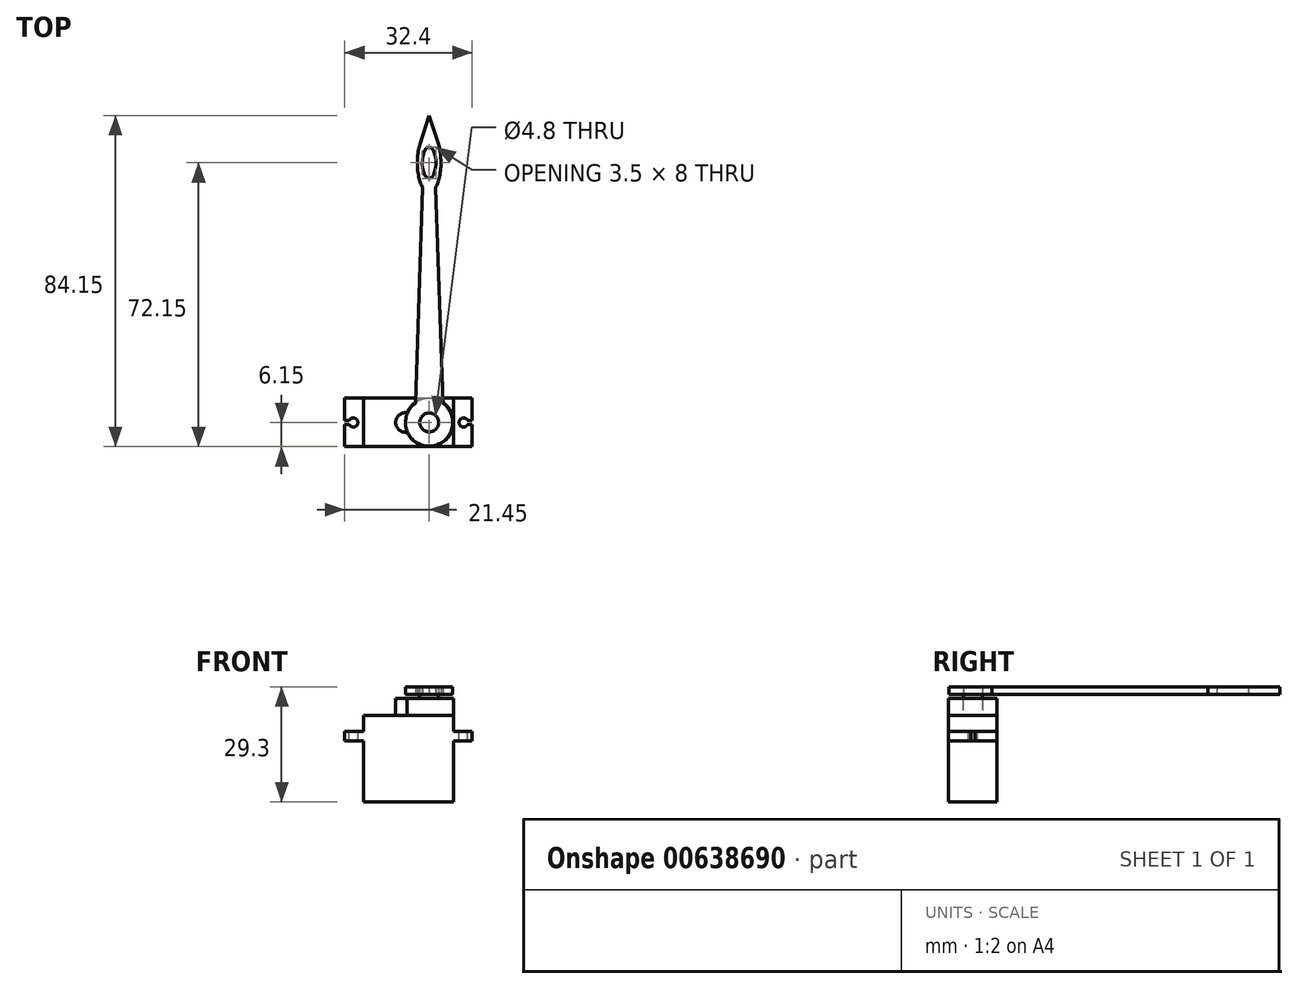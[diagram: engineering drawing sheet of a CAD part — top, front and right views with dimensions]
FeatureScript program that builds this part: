
annotation { "Feature Type Name" : "Feature", "Feature Type Description" : "" }
export const myFeature = defineFeature(function(context is Context, id is Id, definition is map)
    precondition{}
    {
        {
            var Q0;
            Q0=qCreatedBy(makeId("Top.planeOp"),FACE);
            var sketch = newSketch(context, id + "F0", { "sketchPlane" : qUnion([Q0])});
            skLineSegment(sketch, "E0.bottom", {"start": v(0, 0) * mm, "end": v(22.8, 0) * mm});
            skLineSegment(sketch, "E0.top", {"start": v(0, 12.3) * mm, "end": v(22.8, 12.3) * mm});
            skLineSegment(sketch, "E0.left", {"start": v(0, 0) * mm, "end": v(0, 12.3) * mm});
            skLineSegment(sketch, "E0.right", {"start": v(22.8, 0) * mm, "end": v(22.8, 12.3) * mm});
            skSolve(sketch);
        }
        {
            var Q0;
            Q0 = qSketchRegion(id + "F0", true);
            extrude(context, id + "F1", {"entities" : qUnion([Q0]), "depth" : 18 * mm, "offsetDistance" : 25 * mm});
        }
        {
            var Q0;
            Q0=makeQuery(id+"F1.opExtrude","CAP_FACE",FACE,{"disambiguationData":[OSD([sQuery(id+"F0.wireOp",EDGE,"E0.bottom"),sQuery(id+"F0.wireOp",EDGE,"E0.top"),sQuery(id+"F0.wireOp",EDGE,"E0.left"),sQuery(id+"F0.wireOp",EDGE,"E0.right")])],"isStart":false});
            var sketch = newSketch(context, id + "F2", { "sketchPlane" : qUnion([Q0])});
            skLineSegment(sketch, "E1.0", {"start": v(0, 12.3) * mm, "end": v(22.8, 12.3) * mm});
            skLineSegment(sketch, "E2.0", {"start": v(0, 0) * mm, "end": v(22.8, 0) * mm});
            skLineSegment(sketch, "E3", {"start": v(0, 12.3) * mm, "end": v(-4.8, 12.3) * mm});
            skLineSegment(sketch, "E4", {"start": v(-4.8, 12.3) * mm, "end": v(-4.8, 6.65) * mm});
            skLineSegment(sketch, "E5", {"start": v(-4.8, 0) * mm, "end": v(0, 0) * mm});
            skLineSegment(sketch, "E6", {"start": v(22.8, 0) * mm, "end": v(27.6, 0) * mm});
            skLineSegment(sketch, "E7", {"start": v(27.6, 0) * mm, "end": v(27.6, 5.65) * mm});
            skLineSegment(sketch, "E8", {"start": v(27.6, 12.3) * mm, "end": v(22.8, 12.3) * mm});
            skArc(sketch, "E9", {"start": v(-3.64, 5.65) * mm, "mid": v(-1.45, 6.15) * mm, "end": v(-3.64, 6.65) * mm});
            skArc(sketch, "E10", {"start": v(26.44, 6.65) * mm, "mid": v(24.25, 6.15) * mm, "end": v(26.44, 5.65) * mm});
            skPoint(sketch, "E10.centerSnap0", {"position": v(22.8, 6.15) * mm});
            skLineSegment(sketch, "E11", {"start": v(-2.6, 6.15) * mm, "end": v(25.4, 6.15) * mm, "construction": true});
            skLineSegment(sketch, "E12", {"start": v(11.4, 6.15) * mm, "end": v(11.4, 12.3) * mm, "construction": true});
            skLineSegment(sketch, "E13", {"start": v(-4.8, 6.65) * mm, "end": v(-3.64, 6.65) * mm});
            skLineSegment(sketch, "E14", {"start": v(-4.8, 5.65) * mm, "end": v(-3.64, 5.65) * mm});
            skLineSegment(sketch, "E15", {"start": v(26.44, 6.65) * mm, "end": v(27.6, 6.65) * mm});
            skLineSegment(sketch, "E16", {"start": v(26.44, 5.65) * mm, "end": v(27.6, 5.65) * mm});
            skLineSegment(sketch, "E17.trimOffspring", {"start": v(-4.8, 5.65) * mm, "end": v(-4.8, 0) * mm});
            skLineSegment(sketch, "E18.trimOffspring", {"start": v(27.6, 6.65) * mm, "end": v(27.6, 12.3) * mm});
            skSolve(sketch);
        }
        {
            var Q0;
            Q0 = qSketchRegion(id + "F2", true);
            extrude(context, id + "F3", {"entities" : qUnion([Q0]), "operationType" : NewBodyOperationType.ADD, "oppositeDirection" : true, "depth" : 2.5 * mm, "offsetDistance" : 25 * mm});
        }
        {
            var Q0;
            Q0=makeQuery(id+"F3.boolean.opBoolean","MERGE",FACE,{"derivedFrom":[makeQuery(id+"F1.opExtrude","CAP_FACE",FACE,{"disambiguationData":[OSD([sQuery(id+"F0.wireOp",EDGE,"E0.bottom"),sQuery(id+"F0.wireOp",EDGE,"E0.top"),sQuery(id+"F0.wireOp",EDGE,"E0.left"),sQuery(id+"F0.wireOp",EDGE,"E0.right")])],"isStart":false}),makeQuery(id+"F3.opExtrude","CAP_FACE",FACE,{"disambiguationData":[OSD([sQuery(id+"F2.wireOp",EDGE,"E1.0"),sQuery(id+"F2.wireOp",EDGE,"E2.0"),sQuery(id+"F2.wireOp",EDGE,"E3"),sQuery(id+"F2.wireOp",EDGE,"E4"),sQuery(id+"F2.wireOp",EDGE,"E5"),sQuery(id+"F2.wireOp",EDGE,"E6"),sQuery(id+"F2.wireOp",EDGE,"E7"),sQuery(id+"F2.wireOp",EDGE,"E8"),sQuery(id+"F2.wireOp",EDGE,"E9"),sQuery(id+"F2.wireOp",EDGE,"E10")])],"isStart":true})]});
            var sketch = newSketch(context, id + "F4", { "sketchPlane" : qUnion([Q0])});
            skLineSegment(sketch, "E19.0", {"start": v(22.8, 0) * mm, "end": v(22.8, 12.3) * mm});
            skLineSegment(sketch, "E20.0", {"start": v(0, 0) * mm, "end": v(0, 12.3) * mm});
            skSolve(sketch);
        }
        {
            var Q0;
            {var subQ0=sQuery(id+"F4.wireOp",EDGE,"E19.0");Q0=makeQuery(id+"F4.imprint","IMPRINT",FACE,{"disambiguationData":[TD([[makeQuery(id+"F4.imprint","IMPRINT",EDGE,{"derivedFrom":subQ0}),1.0]])]});}
            extrude(context, id + "F5", {"entities" : qUnion([Q0]), "operationType" : NewBodyOperationType.ADD, "depth" : 4 * mm, "offsetDistance" : 25 * mm});
        }
        {
            var Q0;
            Q0=makeQuery(id+"F5.opExtrude","CAP_FACE",FACE,{"disambiguationData":[OSD([sQuery(id+"F0.wireOp",EDGE,"E0.bottom"),sQuery(id+"F0.wireOp",EDGE,"E0.top"),sQuery(id+"F2.wireOp",EDGE,"E1.0"),sQuery(id+"F2.wireOp",EDGE,"E2.0"),sQuery(id+"F2.wireOp",EDGE,"E3"),sQuery(id+"F2.wireOp",EDGE,"E5"),sQuery(id+"F2.wireOp",EDGE,"E6"),sQuery(id+"F2.wireOp",EDGE,"E8"),sQuery(id+"F4.wireOp",EDGE,"E19.0"),sQuery(id+"F4.wireOp",EDGE,"E20.0")])],"isStart":false});
            var sketch = newSketch(context, id + "F6", { "sketchPlane" : qUnion([Q0])});
            skArc(sketch, "E21", {"start": v(11.03, 3.65) * mm, "mid": v(22.8, 6.15) * mm, "end": v(11.03, 8.65) * mm});
            skPoint(sketch, "E21.first.point", {"position": v(16.65, 0) * mm});
            skPoint(sketch, "E21.second.point", {"position": v(22.8, 6.15) * mm});
            skPoint(sketch, "E21.third.point", {"position": v(16.65, 12.3) * mm});
            skArc(sketch, "E22", {"start": v(10.65, 8.65) * mm, "mid": v(8.15, 6.15) * mm, "end": v(10.65, 3.65) * mm});
            skLineSegment(sketch, "E23", {"start": v(10.65, 8.65) * mm, "end": v(11.03, 8.65) * mm});
            skLineSegment(sketch, "E24", {"start": v(10.65, 3.65) * mm, "end": v(11.03, 3.65) * mm});
            skSolve(sketch);
        }
        {
            var Q0;
            Q0 = qSketchRegion(id + "F6", true);
            extrude(context, id + "F7", {"entities" : qUnion([Q0]), "operationType" : NewBodyOperationType.ADD, "depth" : 4.3 * mm, "offsetDistance" : 25 * mm});
        }
        {
            var Q0;
            Q0=makeQuery(id+"F7.opExtrude","CAP_FACE",FACE,{"disambiguationData":[OSD([sQuery(id+"F6.wireOp",EDGE,"E21"),sQuery(id+"F6.wireOp",EDGE,"E22"),sQuery(id+"F6.wireOp",EDGE,"E23"),sQuery(id+"F6.wireOp",EDGE,"E24")])],"isStart":false});
            var sketch = newSketch(context, id + "F8", { "sketchPlane" : qUnion([Q0])});
            skCircle(sketch, "E25", {"center": v(16.65, 6.15) * mm, "radius": 2.4 * mm});
            skSolve(sketch);
        }
        {
            var Q0;
            Q0 = qSketchRegion(id + "F8", true);
            extrude(context, id + "F9", {"entities" : qUnion([Q0]), "operationType" : NewBodyOperationType.ADD, "depth" : 2.9 * mm, "offsetDistance" : 25 * mm});
        }
        {
            var Q0;
            Q0=makeQuery(id+"F7.opExtrude","CAP_FACE",FACE,{"disambiguationData":[OSD([sQuery(id+"F6.wireOp",EDGE,"E21"),sQuery(id+"F6.wireOp",EDGE,"E22"),sQuery(id+"F6.wireOp",EDGE,"E23"),sQuery(id+"F6.wireOp",EDGE,"E24")])],"isStart":false});
            cPlane(context, id + "F10", {"entities" : qUnion([Q0]), "cplaneType" : CPlaneType.OFFSET, "offset" : 1 * mm, "width" : 150 * mm, "height" : 150 * mm});
        }
        {
            var Q0;
            Q0=qCreatedBy(id+"F10.planeOp",FACE);
            var sketch = newSketch(context, id + "F11", { "sketchPlane" : qUnion([Q0])});
            skCircle(sketch, "E26.0", {"center": v(16.65, 6.15) * mm, "radius": 2.4 * mm, "construction": true});
            skCircle(sketch, "E27", {"center": v(16.65, 6.15) * mm, "radius": 6 * mm});
            skCircle(sketch, "E28", {"center": v(16.65, 6.15) * mm, "radius": 2.4 * mm});
            skLineSegment(sketch, "E29", {"start": v(13.15, 11.02) * mm, "end": v(15.04, 65.83) * mm});
            skLineSegment(sketch, "E30", {"start": v(15.15, 69.15) * mm, "end": v(18.15, 69.15) * mm, "construction": true});
            skLineSegment(sketch, "E31", {"start": v(18.26, 65.83) * mm, "end": v(20.15, 11.02) * mm});
            skLineSegment(sketch, "E32", {"start": v(16.65, 69.15) * mm, "end": v(16.65, 6.15) * mm, "construction": true});
            skEllipticalArc(sketch, "E33", {});
            skLineSegment(sketch, "E34", {"start": v(14.3, 76.84) * mm, "end": v(16.65, 84.15) * mm});
            skLineSegment(sketch, "E35", {"start": v(16.65, 84.15) * mm, "end": v(19, 76.84) * mm});
            skLineSegment(sketch, "E36", {"start": v(16.65, 84.15) * mm, "end": v(16.65, 69.15) * mm, "construction": true});
            skEllipse(sketch, "E37", {"center": v(16.65, 72.15) * mm, "majorRadius": 4 * mm, "minorRadius": 1.75 * mm, "majorAxis": v(0, 1)});
            skEllipticalArc(sketch, "E38.trimOffspring", {});
            const initialGuessF11  = {"E33": [0.01665, 0.07215, 0, -1, 0.0075, 0.003, 4.037257447447658, 5.715008225795697], "E38.trimOffspring": [0.01665, 0.07215, 0, -1, 0.0075, 0.003, 0.5681770813838886, 2.245927859731928]};
            skSetInitialGuess(sketch, initialGuessF11);
            skSolve(sketch);
        }
        {
            var Q0;
            Q0 = qSketchRegion(id + "F11", true);
            extrude(context, id + "F12", {"entities" : qUnion([Q0]), "depth" : 2 * mm, "offsetDistance" : 25 * mm});
        }
    });
